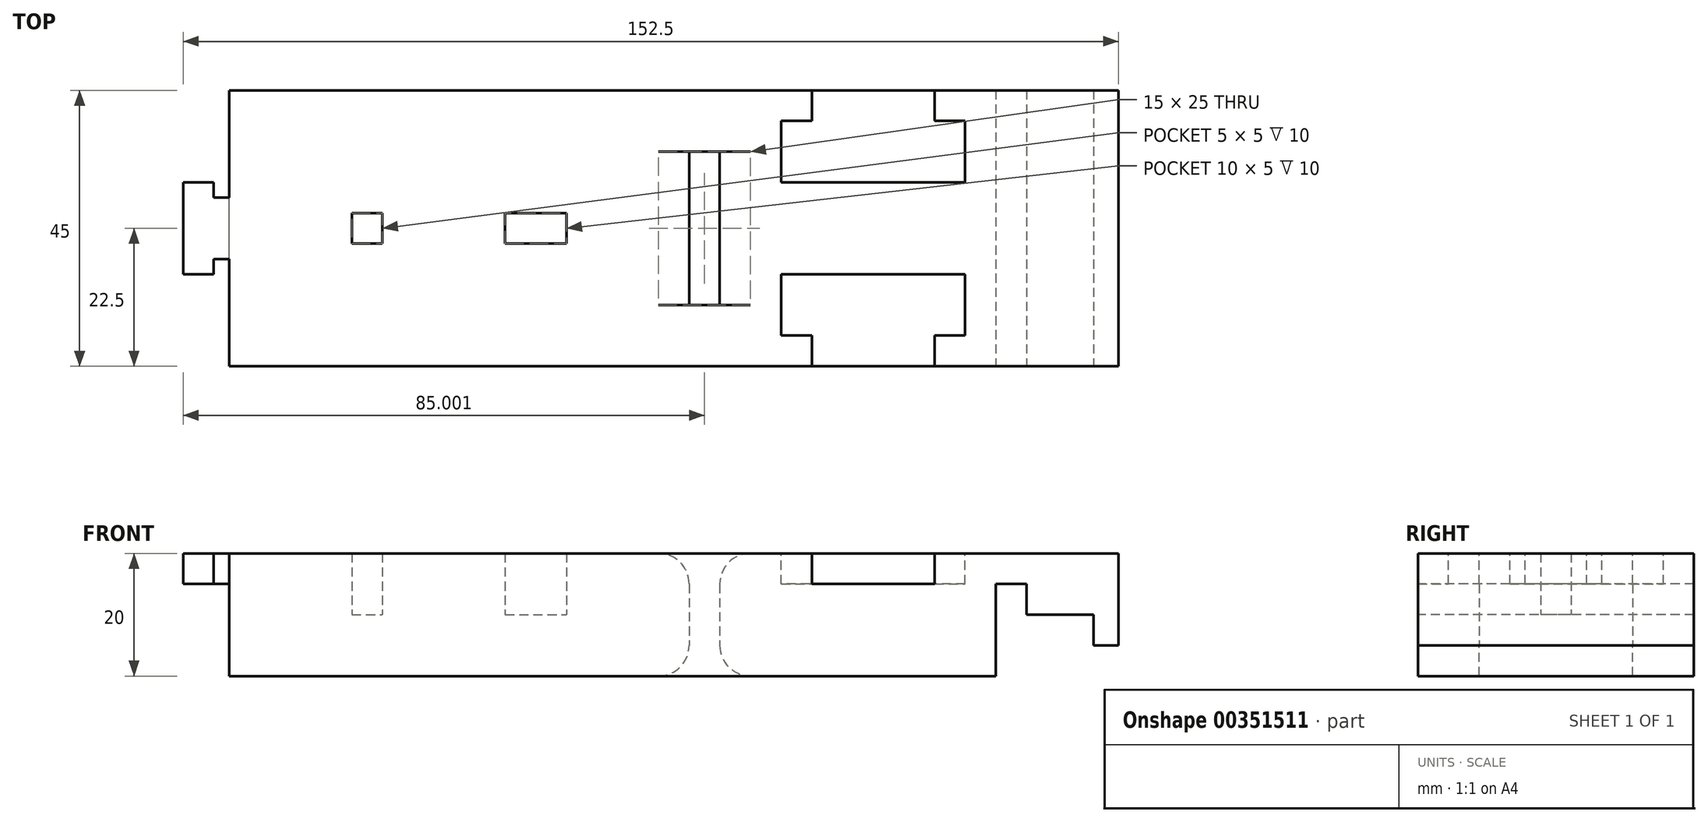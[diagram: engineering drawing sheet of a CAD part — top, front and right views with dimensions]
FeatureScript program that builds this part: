
annotation { "Feature Type Name" : "Feature", "Feature Type Description" : "" }
export const myFeature = defineFeature(function(context is Context, id is Id, definition is map)
    precondition{}
    {
        {
            var Q0;
            Q0=qCreatedBy(makeId("Top.planeOp"),FACE);
            var sketch = newSketch(context, id + "F0", { "sketchPlane" : qUnion([Q0])});
            skLineSegment(sketch, "E0.bottom", {"start": v(-46.9, 0) * mm, "end": v(98.1, 0) * mm});
            skLineSegment(sketch, "E0.top", {"start": v(-46.9, 45) * mm, "end": v(98.1, 45) * mm});
            skLineSegment(sketch, "E0.left", {"start": v(-46.9, 0) * mm, "end": v(-46.9, 45) * mm});
            skLineSegment(sketch, "E0.right", {"start": v(98.1, 0) * mm, "end": v(98.1, 45) * mm});
            skLineSegment(sketch, "E1", {"start": v(-46.9, 45) * mm, "end": v(-46.9, 27.5) * mm, "construction": true});
            skLineSegment(sketch, "E2", {"start": v(-46.9, 27.5) * mm, "end": v(-49.4, 27.5) * mm});
            skLineSegment(sketch, "E3", {"start": v(-46.9, 0) * mm, "end": v(-46.9, 17.5) * mm, "construction": true});
            skLineSegment(sketch, "E4", {"start": v(-46.9, 17.5) * mm, "end": v(-49.4, 17.5) * mm});
            skLineSegment(sketch, "E5", {"start": v(-49.4, 17.5) * mm, "end": v(-49.4, 15) * mm});
            skLineSegment(sketch, "E6", {"start": v(-49.4, 15) * mm, "end": v(-54.4, 15) * mm});
            skLineSegment(sketch, "E7", {"start": v(-54.4, 15) * mm, "end": v(-54.4, 30) * mm});
            skLineSegment(sketch, "E8", {"start": v(-54.4, 30) * mm, "end": v(-49.4, 30) * mm});
            skLineSegment(sketch, "E9", {"start": v(-49.4, 30) * mm, "end": v(-49.4, 27.5) * mm});
            skLineSegment(sketch, "E10", {"start": v(-46.9, 45) * mm, "end": v(-26.9, 45) * mm, "construction": true});
            skLineSegment(sketch, "E11", {"start": v(-26.9, 45) * mm, "end": v(-26.9, 25) * mm, "construction": true});
            skLineSegment(sketch, "E12.bottom", {"start": v(-26.9, 25) * mm, "end": v(-21.9, 25) * mm});
            skLineSegment(sketch, "E12.top", {"start": v(-26.9, 20) * mm, "end": v(-21.9, 20) * mm});
            skLineSegment(sketch, "E12.left", {"start": v(-26.9, 25) * mm, "end": v(-26.9, 20) * mm});
            skLineSegment(sketch, "E12.right", {"start": v(-21.9, 25) * mm, "end": v(-21.9, 20) * mm});
            skLineSegment(sketch, "E13", {"start": v(-21.9, 25) * mm, "end": v(-1.9, 25) * mm, "construction": true});
            skLineSegment(sketch, "E14.bottom", {"start": v(-1.9, 25) * mm, "end": v(8.1, 25) * mm});
            skLineSegment(sketch, "E14.top", {"start": v(-1.9, 20) * mm, "end": v(8.1, 20) * mm});
            skLineSegment(sketch, "E14.left", {"start": v(-1.9, 25) * mm, "end": v(-1.9, 20) * mm});
            skLineSegment(sketch, "E14.right", {"start": v(8.1, 25) * mm, "end": v(8.1, 20) * mm});
            skLineSegment(sketch, "E15", {"start": v(8.1, 25) * mm, "end": v(28.1, 25) * mm, "construction": true});
            skLineSegment(sketch, "E16", {"start": v(28.1, 25) * mm, "end": v(28.1, 35) * mm});
            skLineSegment(sketch, "E17", {"start": v(28.1, 35) * mm, "end": v(33.1, 35) * mm});
            skLineSegment(sketch, "E18", {"start": v(33.1, 35) * mm, "end": v(33.1, 10) * mm});
            skLineSegment(sketch, "E19", {"start": v(33.1, 10) * mm, "end": v(28.1, 10) * mm});
            skLineSegment(sketch, "E20", {"start": v(28.1, 10) * mm, "end": v(28.1, 25) * mm});
            skSolve(sketch);
        }
        {
            var Q0;
            {var subQ3=sQuery(id+"F0.wireOp",EDGE,"E0.bottom");Q0=makeQuery(id+"F0.imprint","IMPRINT",FACE,{"disambiguationData":[TD([[makeQuery(id+"F0.imprint","IMPRINT",EDGE,{"derivedFrom":subQ3}),1.0]])]});}
            extrude(context, id + "F1", {"entities" : qUnion([Q0]), "depth" : 20 * mm});
        }
        {
            var Q0;
            Q0=makeQuery(id+"F0.imprint","IMPRINT",FACE,{"disambiguationData":[TD([[makeQuery(id+"F0.imprint","IMPRINT",EDGE,{"derivedFrom":sQuery(id+"F0.wireOp",EDGE,"E12.bottom")}),-1.0]])]});
            var Q1;
            Q1=makeQuery(id+"F0.imprint","IMPRINT",FACE,{"disambiguationData":[TD([[makeQuery(id+"F0.imprint","IMPRINT",EDGE,{"derivedFrom":sQuery(id+"F0.wireOp",EDGE,"E14.bottom")}),-1.0]])]});
            extrude(context, id + "F2", {"entities" : qUnion([Q0, Q1]), "operationType" : NewBodyOperationType.ADD, "depth" : 10 * mm});
        }
        {
            var Q0;
            Q0=makeQuery(id+"F1.opExtrude","CAP_EDGE",EDGE,{"disambiguationData":[OSD([sQuery(id+"F0.wireOp",EDGE,"E18")])],"isStart":false});
            var Q1;
            Q1=makeQuery(id+"F1.opExtrude","CAP_EDGE",EDGE,{"disambiguationData":[OSD([sQuery(id+"F0.wireOp",EDGE,"E16"),sQuery(id+"F0.wireOp",EDGE,"E20")])],"isStart":false});
            var Q2;
            Q2=makeQuery(id+"F1.opExtrude","CAP_EDGE",EDGE,{"disambiguationData":[OSD([sQuery(id+"F0.wireOp",EDGE,"E16"),sQuery(id+"F0.wireOp",EDGE,"E20")])],"isStart":true});
            var Q3;
            Q3=makeQuery(id+"F1.opExtrude","CAP_EDGE",EDGE,{"disambiguationData":[OSD([sQuery(id+"F0.wireOp",EDGE,"E18")])],"isStart":true});
            fillet(context, id + "F3", {"entities" : qUnion([Q0, Q1, Q2, Q3]), "radius" : 5 * mm, "tangentPropagation" : true, "allowEdgeOverflow" : false});
        }
        {
            var Q0;
            Q0=makeQuery(id+"F1.opExtrude","CAP_FACE",FACE,{"disambiguationData":[OSD([sQuery(id+"F0.wireOp",EDGE,"E0.bottom"),sQuery(id+"F0.wireOp",EDGE,"E0.top"),sQuery(id+"F0.wireOp",EDGE,"E0.left"),sQuery(id+"F0.wireOp",EDGE,"E0.right"),sQuery(id+"F0.wireOp",EDGE,"E12.bottom"),sQuery(id+"F0.wireOp",EDGE,"E12.top"),sQuery(id+"F0.wireOp",EDGE,"E12.left"),sQuery(id+"F0.wireOp",EDGE,"E12.right"),sQuery(id+"F0.wireOp",EDGE,"E14.bottom"),sQuery(id+"F0.wireOp",EDGE,"E14.top"),sQuery(id+"F0.wireOp",EDGE,"E14.left"),sQuery(id+"F0.wireOp",EDGE,"E14.right"),sQuery(id+"F0.wireOp",EDGE,"E16"),sQuery(id+"F0.wireOp",EDGE,"E17"),sQuery(id+"F0.wireOp",EDGE,"E18"),sQuery(id+"F0.wireOp",EDGE,"E19"),sQuery(id+"F0.wireOp",EDGE,"E20")])],"isStart":false});
            var sketch = newSketch(context, id + "F4", { "sketchPlane" : qUnion([Q0])});
            skLineSegment(sketch, "E21", {"start": v(-46.9, 45) * mm, "end": v(-46.9, 27.5) * mm, "construction": true});
            skLineSegment(sketch, "E22", {"start": v(-46.9, 27.5) * mm, "end": v(-49.4, 27.5) * mm});
            skLineSegment(sketch, "E23", {"start": v(-49.4, 27.5) * mm, "end": v(-49.4, 30) * mm});
            skLineSegment(sketch, "E24", {"start": v(-49.4, 30) * mm, "end": v(-54.4, 30) * mm});
            skLineSegment(sketch, "E25", {"start": v(-54.4, 30) * mm, "end": v(-54.4, 15) * mm});
            skLineSegment(sketch, "E26", {"start": v(-54.4, 15) * mm, "end": v(-49.4, 15) * mm});
            skPoint(sketch, "E26.endSnap0", {"position": v(-49.4, 28.75) * mm});
            skLineSegment(sketch, "E27", {"start": v(-49.4, 15) * mm, "end": v(-49.4, 17.5) * mm});
            skLineSegment(sketch, "E28", {"start": v(-49.4, 17.5) * mm, "end": v(-46.9, 17.5) * mm});
            skSolve(sketch);
        }
        {
            var Q0;
            {var subQ0=sQuery(id+"F4.wireOp",EDGE,"E22");Q0=makeQuery(id+"F4.imprint","IMPRINT",FACE,{"disambiguationData":[TD([[makeQuery(id+"F4.imprint","IMPRINT",EDGE,{"derivedFrom":subQ0}),1.0]])]});}
            extrude(context, id + "F5", {"entities" : qUnion([Q0]), "operationType" : NewBodyOperationType.ADD, "depth" : -5 * mm});
        }
        {
            var Q0;
            Q0=makeQuery(id+"F1.opExtrude","SWEPT_FACE",FACE,{"disambiguationData":[OSD([sQuery(id+"F0.wireOp",EDGE,"E0.bottom")])]});
            var sketch = newSketch(context, id + "F6", { "sketchPlane" : qUnion([Q0])});
            skLineSegment(sketch, "E29", {"start": v(98.1, 0) * mm, "end": v(93.1, 0) * mm, "construction": true});
            skLineSegment(sketch, "E30", {"start": v(83.1, 10) * mm, "end": v(83.1, 15) * mm});
            skLineSegment(sketch, "E31", {"start": v(83.1, 15) * mm, "end": v(78.1, 15) * mm});
            skLineSegment(sketch, "E32", {"start": v(78.1, 15) * mm, "end": v(78.1, 0) * mm});
            skLineSegment(sketch, "E33", {"start": v(83.1, 10) * mm, "end": v(94, 10) * mm});
            skLineSegment(sketch, "E34", {"start": v(94, 10) * mm, "end": v(94, 5) * mm});
            skLineSegment(sketch, "E35", {"start": v(94, 5) * mm, "end": v(98.1, 5) * mm});
            skSolve(sketch);
        }
        {
            var Q0;
            Q0 = qSketchRegion(id + "F6", true);
            var Q1;
            Q1=makeQuery(id+"F6.imprint","IMPRINT",FACE,{"disambiguationData":[TD([[makeQuery(id+"F6.imprint","IMPRINT",EDGE,{"derivedFrom":sQuery(id+"F6.wireOp",EDGE,"E30")}),1.0]])]});
            extrude(context, id + "F7", {"entities" : qUnion([Q0, Q1]), "operationType" : NewBodyOperationType.REMOVE, "oppositeDirection" : true, "depth" : 50 * mm});
        }
        {
            var Q0;
            {var subQ0=sQuery(id+"F0.wireOp",EDGE,"E0.left");Q0=makeQuery(id+"F5.boolean.opBoolean","MERGE",FACE,{"derivedFrom":[makeQuery(id+"F1.opExtrude","CAP_FACE",FACE,{"disambiguationData":[OSD([sQuery(id+"F0.wireOp",EDGE,"E0.bottom"),sQuery(id+"F0.wireOp",EDGE,"E0.top"),subQ0,sQuery(id+"F0.wireOp",EDGE,"E0.right"),sQuery(id+"F0.wireOp",EDGE,"E12.bottom"),sQuery(id+"F0.wireOp",EDGE,"E12.top"),sQuery(id+"F0.wireOp",EDGE,"E12.left"),sQuery(id+"F0.wireOp",EDGE,"E12.right"),sQuery(id+"F0.wireOp",EDGE,"E14.bottom"),sQuery(id+"F0.wireOp",EDGE,"E14.top"),sQuery(id+"F0.wireOp",EDGE,"E14.left"),sQuery(id+"F0.wireOp",EDGE,"E14.right"),sQuery(id+"F0.wireOp",EDGE,"E16"),sQuery(id+"F0.wireOp",EDGE,"E17"),sQuery(id+"F0.wireOp",EDGE,"E18"),sQuery(id+"F0.wireOp",EDGE,"E19"),sQuery(id+"F0.wireOp",EDGE,"E20")])],"isStart":false}),makeQuery(id+"F5.opExtrude","CAP_FACE",FACE,{"disambiguationData":[OSD([subQ0,sQuery(id+"F4.wireOp",EDGE,"E22"),sQuery(id+"F4.wireOp",EDGE,"E23"),sQuery(id+"F4.wireOp",EDGE,"E24"),sQuery(id+"F4.wireOp",EDGE,"E25"),sQuery(id+"F4.wireOp",EDGE,"E26"),sQuery(id+"F4.wireOp",EDGE,"E27"),sQuery(id+"F4.wireOp",EDGE,"E28")])],"isStart":true})]});}
            var sketch = newSketch(context, id + "F8", { "sketchPlane" : qUnion([Q0])});
            skLineSegment(sketch, "E36", {"start": v(98.1, 45) * mm, "end": v(68.1, 45) * mm, "construction": true});
            skLineSegment(sketch, "E37", {"start": v(68.1, 45) * mm, "end": v(68.1, 40) * mm});
            skLineSegment(sketch, "E38", {"start": v(68.1, 40) * mm, "end": v(73.1, 40) * mm});
            skLineSegment(sketch, "E39", {"start": v(73.1, 40) * mm, "end": v(73.1, 30) * mm});
            skLineSegment(sketch, "E40", {"start": v(73.1, 30) * mm, "end": v(43.1, 30) * mm});
            skLineSegment(sketch, "E41", {"start": v(43.1, 30) * mm, "end": v(43.1, 40) * mm});
            skLineSegment(sketch, "E42", {"start": v(43.1, 40) * mm, "end": v(48.1, 40) * mm});
            skLineSegment(sketch, "E43", {"start": v(48.1, 40) * mm, "end": v(48.1, 45) * mm});
            skLineSegment(sketch, "E44", {"start": v(48.1, 45) * mm, "end": v(68.1, 45) * mm});
            skLineSegment(sketch, "E45", {"start": v(68.1, 45) * mm, "end": v(68.1, 0) * mm, "construction": true});
            skPoint(sketch, "E45.endSnap0", {"position": v(68.1, 42.5) * mm});
            skLineSegment(sketch, "E46", {"start": v(68.1, 0) * mm, "end": v(48.1, 0) * mm, "construction": true});
            skLineSegment(sketch, "E47", {"start": v(48.1, 0) * mm, "end": v(48.1, 5) * mm});
            skLineSegment(sketch, "E48", {"start": v(48.1, 5) * mm, "end": v(43.1, 5) * mm});
            skLineSegment(sketch, "E49", {"start": v(43.1, 5) * mm, "end": v(43.1, 15) * mm});
            skLineSegment(sketch, "E50", {"start": v(43.1, 15) * mm, "end": v(73.1, 15) * mm});
            skLineSegment(sketch, "E51", {"start": v(73.1, 15) * mm, "end": v(73.1, 5) * mm});
            skLineSegment(sketch, "E52", {"start": v(73.1, 5) * mm, "end": v(68.1, 5) * mm});
            skLineSegment(sketch, "E53", {"start": v(68.1, 5) * mm, "end": v(68.1, 0) * mm});
            skLineSegment(sketch, "E54", {"start": v(48.1, 0) * mm, "end": v(68.1, 0) * mm});
            skSolve(sketch);
        }
        {
            var Q0;
            Q0=makeQuery(id+"F8.imprint","IMPRINT",FACE,{"disambiguationData":[TD([[makeQuery(id+"F8.imprint","IMPRINT",EDGE,{"derivedFrom":sQuery(id+"F8.wireOp",EDGE,"E47")}),-1.0]])]});
            var Q1;
            Q1=makeQuery(id+"F8.imprint","IMPRINT",FACE,{"disambiguationData":[TD([[makeQuery(id+"F8.imprint","IMPRINT",EDGE,{"derivedFrom":sQuery(id+"F8.wireOp",EDGE,"E37")}),-1.0]])]});
            extrude(context, id + "F9", {"entities" : qUnion([Q0, Q1]), "operationType" : NewBodyOperationType.REMOVE, "oppositeDirection" : true, "depth" : 5 * mm});
        }
    });
